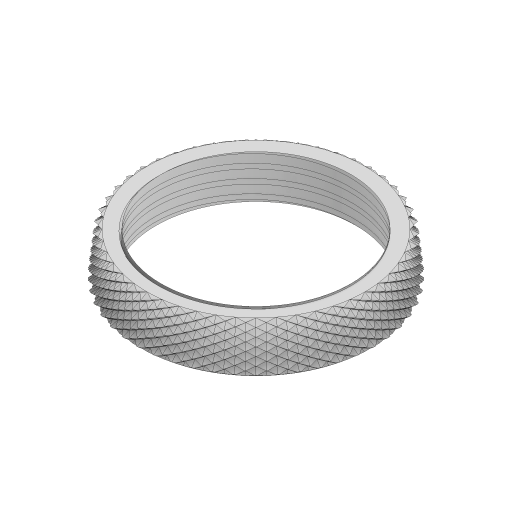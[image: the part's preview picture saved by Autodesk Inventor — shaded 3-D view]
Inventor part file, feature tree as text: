
AUTODESK INVENTOR PART (.ipt)
format: ipt  version: 2023 (Build 270158000, 158)  size: 9,574,912 bytes
history: native  units: mm
features: sketch x5, helix x3, draft x2, extrude x1, pattern_circular x1, mirror x1, revolve x1, projected_geometry x1
ambient origin geometry x8: Origin, YZ Plane, XZ Plane, XY Plane, X Axis, Y Axis, Z Axis, Center Point
bodies: Solid1 (feature_tree)
feature tree (15):
  extrude  "Extrusion1"  Depth=6.52mm TaperAngle=0.0deg
  draft  "FaceDraft1"
  sketch  "Sketch2"  dims[d7=2.0mm d8=9.0mm d9=10.0mm d10=1.047198mm d11=90.0deg d12=90.0deg d13=0.0mm d14=0.0mm d15=2.0mm d16=3.0mm d17=10.0mm d18=-1.047198mm d19=90.0deg d20=90.0deg d21=0.0mm d22=0.0mm d23=3.5mm d91=1.047198mm d109=1.308997mm]
  sketch  "Sketch4"  dims[d112=2.0mm d113=6.52mm d114=1.25mm d115=1.047198mm]
  helix  "Coil1"  [1 undecoded]
  helix  "Coil2"  [1 undecoded]
  draft  "FaceDraft2"
  helix  "Coil10"  [1 undecoded]
  pattern_circular  "Circular Pattern5"  Count=48 Angle=360.0deg
  mirror  "Mirror1"
  revolve  "Revolution2"  [1 undecoded]
  sketch  "Sketch1"  dims[d0=26.5mm d2=6.52mm d3=0.0mm d4=1.047198mm]
  sketch  "Sketch13"  dims[d116=90.0deg d117=90.0deg d118=0.0mm d119=0.0mm d122=480.0mm d123=360.0deg]
  sketch  "Sketch14"  dims[d127=60.0deg d128=15.211695mm d129=360.0deg d130=8.726646mm]
  projected_geometry  "Project Cut Edges1"
note: 4 required parameter values undecoded (feature->parameter linkage not recoverable at this tier; creation-order binding heuristic only, values carry confidence <= 0.55)